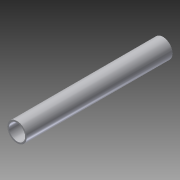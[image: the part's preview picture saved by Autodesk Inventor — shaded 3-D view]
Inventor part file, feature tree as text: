
AUTODESK INVENTOR PART (.ipt)
format: ipt  version: 2015 (Build 190159000, 159)  size: 77,312 bytes
history: native  units: in
note: dims shown in document units (in); Inventor stores cm internally (conversion verified against a paired STEP export)
features: extrude x1, sketch x1
ambient origin geometry x8: Origin, YZ Plane, XZ Plane, XY Plane, X Axis, Y Axis, Z Axis, Center Point
bodies: Solid1 (feature_tree)
feature tree (2):
  extrude  "Extrusion1"  Depth=18.0in
  sketch  "Sketch1"  dims[d0=2.0in d1=2.375in d2=18.0in d3=0.0in]
